# Revit family: QF_ELECTROLUXPROFESSIONAL_1LSNLD_IC64821R_G
name_source: partatom
category: Attrezzature speciali
units: mm (PartAtom-declared; Revit-internal decimal feet)

## family parameters
Basato su piano di lavoro = No
Condiviso = No
Punto di calcolo locali = No
Quota connettore circolare = Usa diametro
Sempre verticale = Sì
Taglio con vuoti quando caricato = No
Tipo di parte = Normale

## types (4) — shared parameters
Depth Actual = 1620 mm
Gas KW = 44
Height Actual = 1270 mm  [stored 4.16667 ft]
Latent Heat Output = 0.0
Length Actual = 2785 mm  [stored 9.13714 ft]
Modello = IC64821R
Phase = 3
Produttore = Electrolux Professional
Sensible Heat Output = 0.0
URL = www.electroluxprofessional.com
Weight = 940
zero-valued in all types: Prospetto di default, Steam Pounds per Hour

## per-type parameters (varying)
| type | Cycle | Descrizione | Item Number | Volts | Watts |
| 9882030275 | 60 Hz | IRONER CYLINDER IC64821R REAR DELIVERY 2120MM ACTIVE GAS CE 208-240/60/3 6MM SST CYL. EN, ES, PO FEED NOW | 1L0H8R | 240 V | 1400 W |
| 9882030189 | 50 Hz | IRONER CYLINDER IC64821R REAR DELIVERY 2120MM SUPERIOR GAS CE 400/50/3 DUBIXIUM FR FEED ALONE VAC.FEED.TABLE | 1L0GSV | 400 V | 1200 W |
| 9882030297 | 50 Hz | IRONER CYLINDER IC64821R REAR DELIVERY 2120MM PERFORMANCE GAS CE 400/50/3 DUBIXIUM FR VAC.FEED.TABLE | 1L82C9 | 400 V | 1200 W |
| 9882030234 | 50 Hz | IRONER CYLINDER IC64821R REAR DELIVERY 2120MM SUPERIOR GAS CE 400/50/3 DUBIXIUM ML FEED ALONE VAC.FEED.TABLE | 1L827U | 400 V | 1200 W |

note: [stored X ft] marks values corroborated as IEEE doubles in the binary element streams (Revit-internal decimal feet)

## geometry (parser evidence)
native form markers: Sweep x12
no freeform markers — native parametric forms only
